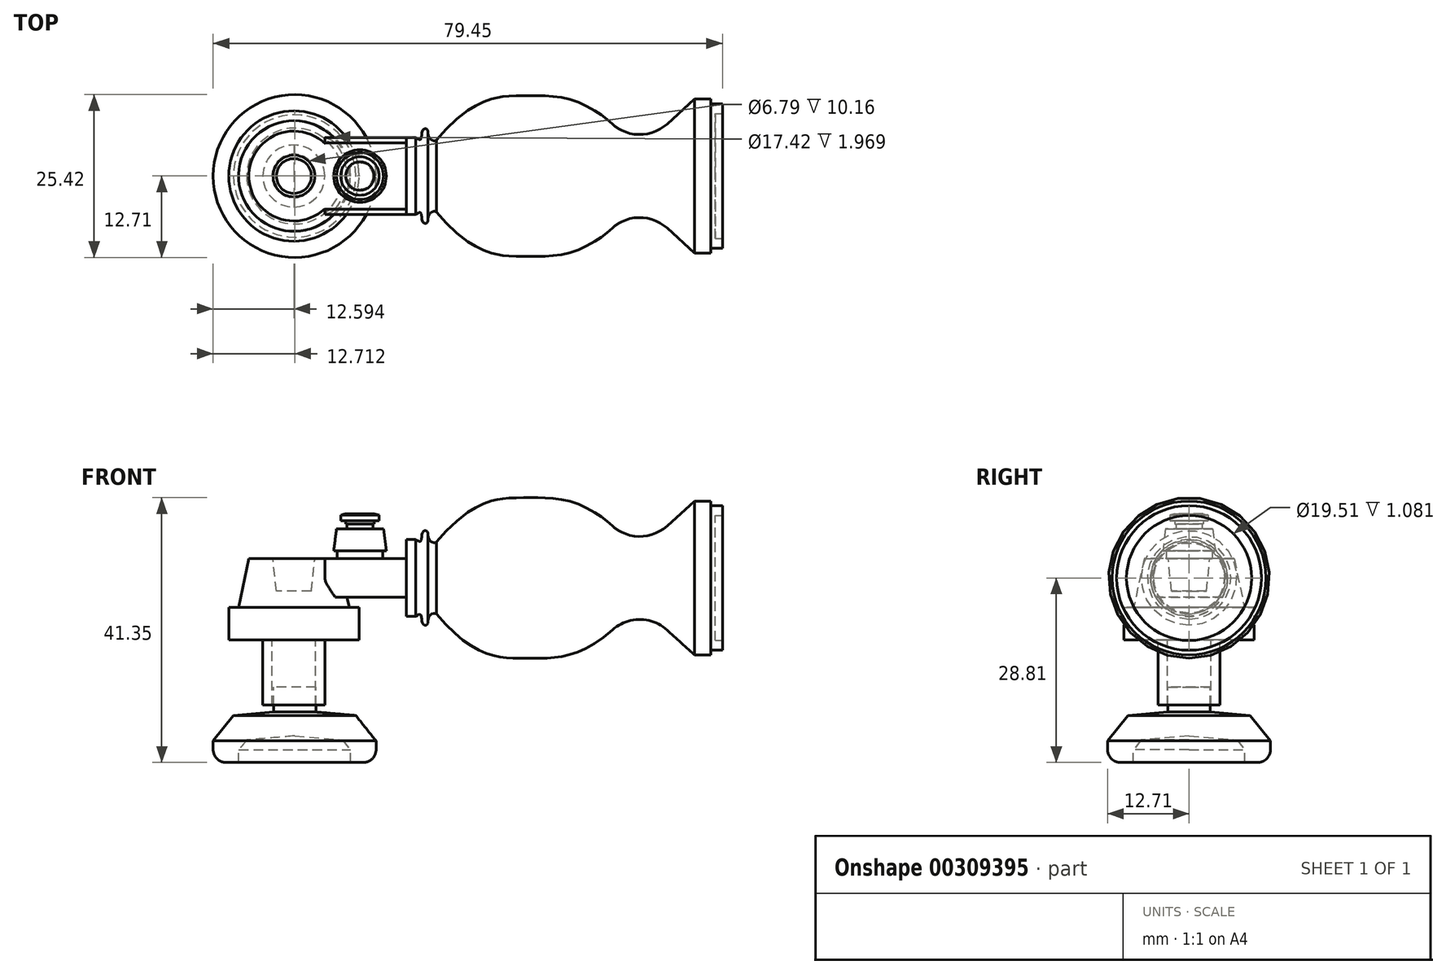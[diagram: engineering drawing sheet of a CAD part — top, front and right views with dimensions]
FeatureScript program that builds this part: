
annotation { "Feature Type Name" : "Feature", "Feature Type Description" : "" }
export const myFeature = defineFeature(function(context is Context, id is Id, definition is map)
    precondition{}
    {
        {
            var Q0;
            Q0=qCreatedBy(makeId("Front.planeOp"),FACE);
            var sketch = newSketch(context, id + "F0", { "sketchPlane" : qUnion([Q0])});
            skFitSpline(sketch, "E0", {"points": [v(4.68, 5.63) * mm, v(18.9, 12.53) * mm, v(36.06, 3.92) * mm], "startDerivative": vector(38.96, 45.6) * mm, "endDerivative": vector(41.46, -52.04) * mm});
            skLineSegment(sketch, "E1", {"start": v(40.69, 8.13) * mm, "end": v(44.95, 12) * mm});
            skLineSegment(sketch, "E2", {"start": v(47.53, 0) * mm, "end": v(0, 0) * mm});
            skLineSegment(sketch, "E3", {"start": v(44.95, 12) * mm, "end": v(47.53, 12) * mm});
            skLineSegment(sketch, "E4", {"start": v(47.53, 12) * mm, "end": v(47.53, 0) * mm});
            skArc(sketch, "E5.filletArc", {"start": v(32.18, 8.1) * mm, "mid": v(36.44, 6.48) * mm, "end": v(40.69, 8.13) * mm});
            skFitSpline(sketch, "E6", {"points": [v(4.68, 5.63) * mm, v(3.95, 5.63) * mm, v(3.4, 6.61) * mm, v(3.37, 7.06) * mm, v(2.97, 7.42) * mm, v(2.52, 7.06) * mm, v(2.43, 6.57) * mm, v(2.13, 5.67) * mm, v(1.45, 6) * mm], "startDerivative": vector(-1.9, -3.52) * mm, "endDerivative": vector(-2.6, 0) * mm});
            skLineSegment(sketch, "E7", {"start": v(0, 0) * mm, "end": v(0, 6) * mm});
            skLineSegment(sketch, "E8", {"start": v(0, 6) * mm, "end": v(1.45, 6) * mm});
            skSolve(sketch);
        }
        {
            var Q0;
            Q0=makeQuery(id+"F0.imprint","IMPRINT",FACE,{"disambiguationData":[TD([[makeQuery(id+"F0.imprint","IMPRINT",EDGE,{"derivedFrom":sQuery(id+"F0.wireOp",EDGE,"E0")}),-1.0]])]});
            var Q1;
            Q1=sQuery(id+"F0.wireOp",EDGE,"E2");
            revolve(context, id + "F1", {"entities" : qUnion([Q0]), "axis" : qUnion([Q1]), "revolveType" : RevolveType.FULL});
        }
        {
            var Q0;
            Q0=qCreatedBy(makeId("Front.planeOp"),FACE);
            var sketch = newSketch(context, id + "F2", { "sketchPlane" : qUnion([Q0])});
            skLineSegment(sketch, "E9", {"start": v(47.53, 0) * mm, "end": v(47.53, 11.29) * mm});
            skLineSegment(sketch, "E10", {"start": v(47.53, 11.29) * mm, "end": v(49.32, 11.29) * mm});
            skLineSegment(sketch, "E11", {"start": v(49.32, 11.29) * mm, "end": v(49.32, 9.76) * mm});
            skLineSegment(sketch, "E12", {"start": v(49.32, 9.76) * mm, "end": v(48.24, 9.76) * mm});
            skLineSegment(sketch, "E13", {"start": v(48.24, 9.76) * mm, "end": v(48.24, 0) * mm});
            skLineSegment(sketch, "E14", {"start": v(48.24, 0) * mm, "end": v(47.53, 0) * mm});
            skSolve(sketch);
        }
        {
            var Q0;
            Q0=makeQuery(id+"F2.imprint","IMPRINT",FACE,{"disambiguationData":[TD([[makeQuery(id+"F2.imprint","IMPRINT",EDGE,{"derivedFrom":sQuery(id+"F2.wireOp",EDGE,"E9")}),-1.0]])]});
            var Q1;
            Q1=sQuery(id+"F2.wireOp",EDGE,"E14");
            revolve(context, id + "F3", {"entities" : qUnion([Q0]), "axis" : qUnion([Q1]), "revolveType" : RevolveType.FULL});
        }
        {
            var Q0;
            Q0=makeQuery(id+"F1.opRevolve","SWEPT_FACE",FACE,{"disambiguationData":[OSD([sQuery(id+"F0.wireOp",EDGE,"E7")])]});
            var sketch = newSketch(context, id + "F4", { "sketchPlane" : qUnion([Q0])});
            skLineSegment(sketch, "E15", {"start": v(-5.2, 3) * mm, "end": v(5.2, 3) * mm});
            skLineSegment(sketch, "E16", {"start": v(-5.2, -3) * mm, "end": v(5.2, -3) * mm});
            skLineSegment(sketch, "E17", {"start": v(0, 0) * mm, "end": v(0, 3) * mm, "construction": true});
            skLineSegment(sketch, "E18", {"start": v(0, 0) * mm, "end": v(0, -3) * mm, "construction": true});
            skArc(sketch, "E19", {"start": v(5.2, 3) * mm, "mid": v(6, 0) * mm, "end": v(5.2, -3) * mm});
            skArc(sketch, "E20", {"start": v(-5.2, -3) * mm, "mid": v(-6, 0) * mm, "end": v(-5.2, 3) * mm});
            skSolve(sketch);
        }
        {
            var Q0;
            Q0 = qSketchRegion(id + "F4", true);
            extrude(context, id + "F5", {"entities" : qUnion([Q0]), "depth" : 12.7 * mm});
        }
        {
            var Q0;
            Q0=makeQuery(id+"F5.opExtrude","SWEPT_FACE",FACE,{"disambiguationData":[OSD([sQuery(id+"F4.wireOp",EDGE,"E15")])]});
            var sketch = newSketch(context, id + "F6", { "sketchPlane" : qUnion([Q0])});
            skCircle(sketch, "E21", {"center": v(-17.54, 0) * mm, "radius": 7.02 * mm});
            skPoint(sketch, "E21.centerSnap0", {"position": v(-12.7, 0) * mm});
            skSolve(sketch);
        }
        {
            var Q0;
            Q0 = qSketchRegion(id + "F6", true);
            extrude(context, id + "F7", {"entities" : qUnion([Q0]), "operationType" : NewBodyOperationType.ADD, "oppositeDirection" : true, "depth" : 7.62 * mm, "hasDraft" : true, "draftAngle" : 12 * degree});
        }
        {
            var Q0;
            Q0=makeQuery(id+"F7.boolean.opBoolean","MERGE",FACE,{"derivedFrom":[makeQuery(id+"F5.opExtrude","SWEPT_FACE",FACE,{"disambiguationData":[OSD([sQuery(id+"F4.wireOp",EDGE,"E15")])]}),makeQuery(id+"F7.opExtrude","CAP_FACE",FACE,{"disambiguationData":[OSD([sQuery(id+"F6.wireOp",EDGE,"E21")])],"isStart":true})]});
            var sketch = newSketch(context, id + "F8", { "sketchPlane" : qUnion([Q0])});
            skCircle(sketch, "E22", {"center": v(-17.54, 0) * mm, "radius": 3.26 * mm});
            skSolve(sketch);
        }
        {
            var Q0;
            Q0=makeQuery(id+"F8.imprint","IMPRINT",FACE,{"disambiguationData":[TD([[makeQuery(id+"F8.imprint","IMPRINT",EDGE,{"derivedFrom":sQuery(id+"F8.wireOp",EDGE,"E22")}),1.0]])]});
            extrude(context, id + "F9", {"entities" : qUnion([Q0]), "operationType" : NewBodyOperationType.REMOVE, "oppositeDirection" : true, "depth" : 5.08 * mm, "hasDraft" : true, "draftAngle" : 6 * degree, "draftPullDirection" : true});
        }
        {
            var Q0;
            Q0=makeQuery(id+"F7.boolean.opBoolean","MERGE",FACE,{"derivedFrom":[makeQuery(id+"F5.opExtrude","SWEPT_FACE",FACE,{"disambiguationData":[OSD([sQuery(id+"F4.wireOp",EDGE,"E15")])]}),makeQuery(id+"F7.opExtrude","CAP_FACE",FACE,{"disambiguationData":[OSD([sQuery(id+"F6.wireOp",EDGE,"E21")])],"isStart":true})]});
            var sketch = newSketch(context, id + "F10", { "sketchPlane" : qUnion([Q0])});
            skCircle(sketch, "E23", {"center": v(-7.22, 0) * mm, "radius": 2.4 * mm});
            skSolve(sketch);
        }
        {
            var Q0;
            Q0=qCreatedBy(makeId("Front.planeOp"),FACE);
            var sketch = newSketch(context, id + "F11", { "sketchPlane" : qUnion([Q0])});
            skPoint(sketch, "E24.0", {"position": v(-7.22, 3) * mm});
            skLineSegment(sketch, "E25", {"start": v(-7.22, 3) * mm, "end": v(-7.22, 16.91) * mm, "construction": true});
            skLineSegment(sketch, "E26", {"start": v(-7.22, 10.03) * mm, "end": v(-5, 10.03) * mm});
            skLineSegment(sketch, "E27", {"start": v(-5, 10.03) * mm, "end": v(-4.22, 9.8) * mm});
            skLineSegment(sketch, "E28", {"start": v(-4.22, 9.8) * mm, "end": v(-4.22, 8.95) * mm});
            skLineSegment(sketch, "E29", {"start": v(-4.22, 8.95) * mm, "end": v(-5, 8.95) * mm});
            skLineSegment(sketch, "E30", {"start": v(-5, 8.95) * mm, "end": v(-5, 8.4) * mm});
            skLineSegment(sketch, "E31", {"start": v(-5, 8.4) * mm, "end": v(-5.18, 8.4) * mm});
            skLineSegment(sketch, "E32", {"start": v(-5.18, 8.4) * mm, "end": v(-5.18, 7.67) * mm});
            skLineSegment(sketch, "E33", {"start": v(-5.18, 7.67) * mm, "end": v(-3.56, 7.67) * mm});
            skLineSegment(sketch, "E34", {"start": v(-3.56, 7.67) * mm, "end": v(-3.12, 4.23) * mm});
            skLineSegment(sketch, "E35", {"start": v(-3.12, 4.23) * mm, "end": v(-3.64, 4.23) * mm});
            skLineSegment(sketch, "E36", {"start": v(-3.64, 4.23) * mm, "end": v(-3.64, 3) * mm});
            skLineSegment(sketch, "E37", {"start": v(-3.64, 3) * mm, "end": v(-7.22, 3) * mm});
            skLineSegment(sketch, "E38", {"start": v(-7.22, 10.03) * mm, "end": v(-7.22, 7.67) * mm});
            skLineSegment(sketch, "E39", {"start": v(-7.22, 7.67) * mm, "end": v(-7.22, 3) * mm});
            skLineSegment(sketch, "E40", {"start": v(-5.18, 7.67) * mm, "end": v(-7.22, 7.67) * mm});
            skSolve(sketch);
        }
        {
            var Q0;
            Q0=makeQuery(id+"F11.imprint","IMPRINT",FACE,{"disambiguationData":[TD([[makeQuery(id+"F11.imprint","IMPRINT",EDGE,{"derivedFrom":sQuery(id+"F11.wireOp",EDGE,"E26")}),-1.0]])]});
            var Q1;
            Q1=sQuery(id+"F11.wireOp",EDGE,"E25");
            revolve(context, id + "F12", {"entities" : qUnion([Q0]), "axis" : qUnion([Q1]), "revolveType" : RevolveType.FULL});
        }
        {
            var Q0;
            Q0=makeQuery(id+"F11.imprint","IMPRINT",FACE,{"disambiguationData":[TD([[makeQuery(id+"F11.imprint","IMPRINT",EDGE,{"derivedFrom":sQuery(id+"F11.wireOp",EDGE,"E33")}),-1.0]])]});
            var Q1;
            Q1=sQuery(id+"F11.wireOp",EDGE,"E25");
            revolve(context, id + "F13", {"entities" : qUnion([Q0]), "axis" : qUnion([Q1]), "revolveType" : RevolveType.FULL});
        }
        {
            var Q0;
            Q0=makeQuery(id+"F7.opExtrude","CAP_FACE",FACE,{"disambiguationData":[OSD([sQuery(id+"F6.wireOp",EDGE,"E21")])],"isStart":false});
            var sketch = newSketch(context, id + "F14", { "sketchPlane" : qUnion([Q0])});
            skCircle(sketch, "E41", {"center": v(-17.54, 0) * mm, "radius": 10.17 * mm});
            skSolve(sketch);
        }
        {
            var Q0;
            Q0 = qSketchRegion(id + "F14", true);
            extrude(context, id + "F15", {"entities" : qUnion([Q0]), "operationType" : NewBodyOperationType.ADD, "depth" : 5.08 * mm});
        }
        {
            var Q0;
            Q0=makeQuery(id+"F15.opExtrude","CAP_FACE",FACE,{"disambiguationData":[OSD([sQuery(id+"F14.wireOp",EDGE,"E41")])],"isStart":false});
            var sketch = newSketch(context, id + "F16", { "sketchPlane" : qUnion([Q0])});
            skCircle(sketch, "E42", {"center": v(-17.54, 0) * mm, "radius": 4.84 * mm});
            skCircle(sketch, "E43", {"center": v(-17.54, 0) * mm, "radius": 3.4 * mm});
            skSolve(sketch);
        }
        {
            var Q0;
            Q0 = qSketchRegion(id + "F16", true);
            extrude(context, id + "F17", {"entities" : qUnion([Q0]), "operationType" : NewBodyOperationType.ADD, "depth" : 10.16 * mm});
        }
        {
            var Q0;
            Q0=qCreatedBy(makeId("Front.planeOp"),FACE);
            var sketch = newSketch(context, id + "F18", { "sketchPlane" : qUnion([Q0])});
            skLineSegment(sketch, "E44", {"start": v(-20.72, -17.05) * mm, "end": v(-17.42, -17.05) * mm});
            skLineSegment(sketch, "E45", {"start": v(-17.42, -17.05) * mm, "end": v(-17.42, -28.81) * mm});
            skLineSegment(sketch, "E46", {"start": v(-17.42, -28.81) * mm, "end": v(-28.1, -28.81) * mm});
            skLineSegment(sketch, "E47", {"start": v(-30.13, -26.78) * mm, "end": v(-30.13, -25.45) * mm});
            skLineSegment(sketch, "E48", {"start": v(-30.13, -25.45) * mm, "end": v(-26.96, -21.47) * mm});
            skLineSegment(sketch, "E49", {"start": v(-26.96, -21.47) * mm, "end": v(-20.72, -20.93) * mm});
            skLineSegment(sketch, "E50", {"start": v(-20.72, -20.93) * mm, "end": v(-20.72, -17.05) * mm});
            skPoint(sketch, "E51.visualSharp", {"position": v(-30.13, -28.81) * mm});
            skArc(sketch, "E51.filletArc", {"start": v(-30.13, -26.78) * mm, "mid": v(-29.53, -28.22) * mm, "end": v(-28.1, -28.81) * mm});
            skSolve(sketch);
        }
        {
            var Q0;
            Q0=makeQuery(id+"F18.imprint","IMPRINT",FACE,{"disambiguationData":[TD([[makeQuery(id+"F18.imprint","IMPRINT",EDGE,{"derivedFrom":sQuery(id+"F18.wireOp",EDGE,"E44")}),-1.0]])]});
            var Q1;
            Q1=sQuery(id+"F18.wireOp",EDGE,"E45");
            revolve(context, id + "F19", {"entities" : qUnion([Q0]), "axis" : qUnion([Q1]), "revolveType" : RevolveType.FULL});
        }
        {
            var Q0;
            Q0=makeQuery(id+"F19.opRevolve","SWEPT_FACE",FACE,{"disambiguationData":[OSD([sQuery(id+"F18.wireOp",EDGE,"E46")])]});
            shell(context, id + "F20", {"entities" : qUnion([Q0]), "thickness" : 4 * mm});
        }
        {
            var Q0;
            Q0=qCreatedBy(makeId("Front.planeOp"),FACE);
            var sketch = newSketch(context, id + "F21", { "sketchPlane" : qUnion([Q0])});
            skLineSegment(sketch, "E52.bottom", {"start": v(-28.69, 17.62) * mm, "end": v(49.15, 17.62) * mm});
            skLineSegment(sketch, "E52.top", {"start": v(-28.69, -28.28) * mm, "end": v(49.15, -28.28) * mm});
            skLineSegment(sketch, "E52.left", {"start": v(-28.69, 17.62) * mm, "end": v(-28.69, -28.28) * mm});
            skLineSegment(sketch, "E52.right", {"start": v(49.15, 17.62) * mm, "end": v(49.15, -28.28) * mm});
            skSolve(sketch);
        }
        {
            var Q0;
            Q0=qCreatedBy(makeId("Right.planeOp"),FACE);
            cPlane(context, id + "F22", {"entities" : qUnion([Q0]), "cplaneType" : CPlaneType.OFFSET, "offset" : 19 * mm, "width" : 150 * mm, "height" : 150 * mm});
        }
        {
            var Q0;
            Q0=qCreatedBy(id+"F22.planeOp",FACE);
            var sketch = newSketch(context, id + "F23", { "sketchPlane" : qUnion([Q0])});
            skArc(sketch, "E53", {"start": v(40.19, -14.12) * mm, "mid": v(24.22, -4.14) * mm, "end": v(5.85, 0) * mm});
            skSolve(sketch);
        }
    });
